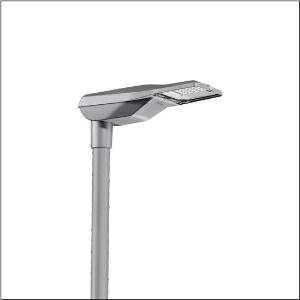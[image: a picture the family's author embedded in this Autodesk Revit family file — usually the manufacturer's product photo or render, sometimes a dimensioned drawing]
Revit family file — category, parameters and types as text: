
# Revit family: streetlight_sl_21_iq_micro___st1_0ab_5xe1m31d08db_7599
name_source: partatom
category: Lighting Fixtures
units: mm (PartAtom-declared; Revit-internal decimal feet)

## family parameters
Cut with Voids When Loaded = No
Host = Face
Light Source = No
Part Type = Normal
Room Calculation Point = No
Round Connector Dimension = Use Diameter
Shared = No

## types (1)
- --- (1 x LED, 4240 lm, 36.4 W, 3000K)
    Apparent Load = 36 VA
    CIE Flux Codes = 38 73 97 100 100
    Color Rendering = 70
    Color Temperature = 3000K
    Default Elevation = 1800 mm
    Description = Streetlight SL 21 iQ micro, mast luminaire, primary light control with lens, of PMMA, primary optical cover: cover, of toughened safety glass, transparent, light distribution: ST1.0aB, light emission: direct distribution, primary light characteristic: asymmetric, installation type: post-top, side-entry, LED, High Power LED, rated luminous flux: 4.240lm, luminous efficacy: 117lm/W, light colour: 730, colour temperature: 3000K, control: Auto-Match, Temp-Guard, Lumen-Switch, Night-Set, Smart-Wire, Light-Fading, Desk-Remote (wireless, voltage-free reading and setting of iQ features in the workshop via application-optimized NFC function/RFID function), optimised constant luminous flux control (CLO 2.0), presetting dimming linear, mains connection: 220..240V, AC, 50/60Hz, start of lifetime: 36W, end of service life: 38W, reduction: 16W, luminaire housing, of diecast aluminium, powder-coated, Siteco® metallic grey (DB 702S), corrosivity category C5 mid according to DIN EN ISO 12944, please order mast flange separately, inclination adjustable: 0°, 5°, 10°, 15°, sealing non-destructively replaceable, multi-level sealing system, length: 528mm, width: 235mm, height: 110mm, mast flange for spigot size: 42mm (side-entry): 5XC10008XM4, 60/48mm (side-entry/post-top): 5XC10108XM2, 76/60mm (side-entry/post-top): 5XC10108XM1, protection rating (complete): IP66, insulation class (complete): insulation class II (safety insulation), certification: CE, ENEC, ENEC+, VDE, impact resistance: IK09, permissible operating ambient temperature for outdoor applications: -40..+50°C, standard-compliant lighting for roads and squares, packaging unit: 1 piece

Light Distribution: ST1.0aB
    Height = 110 mm
    Lamp = 1 x LED
    Lamp Light Flux = 4240 lm
    Lamp Power = 36.4 W
    Lamp count = 1
    Length = 528 mm
    Luminous efficacy = 116 lm/W
    Manufacturer = Siteco
    ModVariant = No
    Model = 5XE1M31D08DB
    Number of Poles = 1
    OnlyDefault = Yes
    Power Factor = 1
    Product Name = Streetlight SL 21 iQ micro | ST1.0aB
    Product group = mast luminaire | pylon top
    ProductGroupID = 6100
    Protection Class = Protection class II
    Protection Degree = IP 66
    RLX_Detail_Level = 1
    RLX_Emergency_Light_Flux = 0 lm
    RLX_Emergency_Type = 0
    RLX_Emergency_Type_DB = No
    RlxData = <blob elided: 99981 chars, md5=aeea8c6f>
    Socket = socket
    Standby Power = 0 W
    System Light Flux = 4240 lm
    System Power = 36 W
    Type Comments = factory setting: luminous flux: 100 % | dim-lin: 254 | 715 mA
    Type Image = l_1006881.jpg
    URL = http://relux.com
    VarID = @adj_104247
    Voltage = 0 V
    Weight = 0.00 kg
    Width = 235 mm

## geometry (parser evidence)
native form markers: Blend x4, Sweep x9
no freeform markers — native parametric forms only
